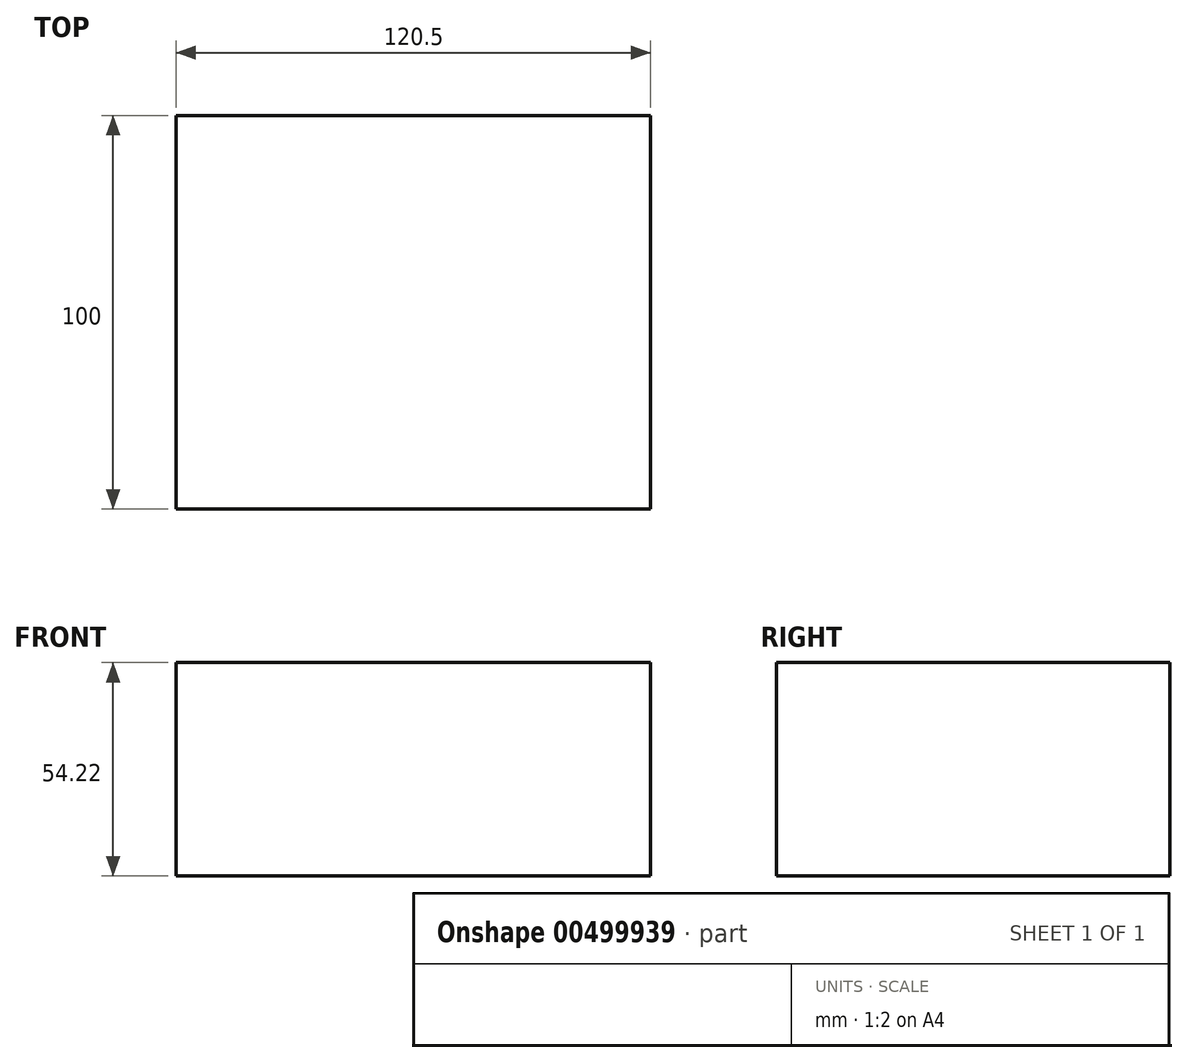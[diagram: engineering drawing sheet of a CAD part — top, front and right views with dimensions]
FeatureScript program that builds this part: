
annotation { "Feature Type Name" : "Feature", "Feature Type Description" : "" }
export const myFeature = defineFeature(function(context is Context, id is Id, definition is map)
    precondition{}
    {
        {
            var Q0;
            Q0=qCreatedBy(makeId("Front.planeOp"),FACE);
            var sketch = newSketch(context, id + "F0", { "sketchPlane" : qUnion([Q0])});
            skLineSegment(sketch, "E0.bottom", {"start": v(-60.25, 27.11) * mm, "end": v(60.25, 27.11) * mm});
            skLineSegment(sketch, "E0.top", {"start": v(-60.25, -27.11) * mm, "end": v(60.25, -27.11) * mm});
            skLineSegment(sketch, "E0.left", {"start": v(-60.25, 27.11) * mm, "end": v(-60.25, -27.11) * mm});
            skLineSegment(sketch, "E0.right", {"start": v(60.25, 27.11) * mm, "end": v(60.25, -27.11) * mm});
            skPoint(sketch, "E0.middle", {"position": v(0, 0) * mm});
            skSolve(sketch);
        }
        {
            var Q0;
            Q0=makeQuery(id+"F0.imprint","IMPRINT",FACE,{"disambiguationData":[TD([[makeQuery(id+"F0.imprint","IMPRINT",EDGE,{"derivedFrom":sQuery(id+"F0.wireOp",EDGE,"E0.bottom")}),-1.0]])]});
            extrude(context, id + "F1", {"entities" : qUnion([Q0]), "depth" : 100 * mm});
        }
    });
